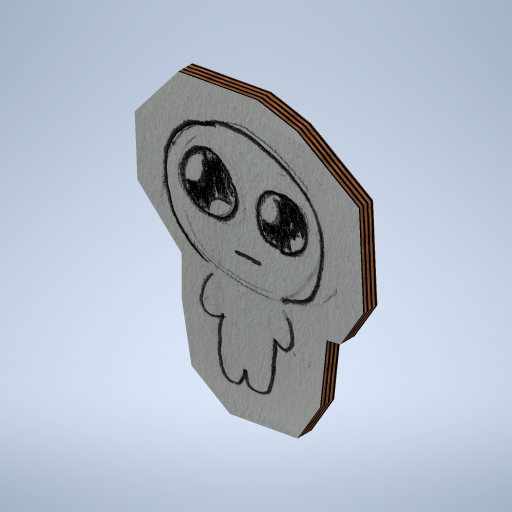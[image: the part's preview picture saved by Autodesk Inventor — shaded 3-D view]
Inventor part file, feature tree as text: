
AUTODESK INVENTOR PART (.ipt)
format: ipt  version: 2023 (Build 270158000, 158)  size: 1,415,680 bytes
history: native  units: in
note: dims shown in document units (in); Inventor stores cm internally (conversion verified against a paired STEP export)
features: extrude x1, sketch x1
ambient origin geometry x8: Origin, YZ Plane, XZ Plane, XY Plane, X Axis, Y Axis, Z Axis, Center Point
bodies: Solid1 (feature_tree)
feature tree (2):
  extrude  "Extrusion1"  Depth=1.0in
  sketch  "Sketch1"  dims[d8=1.0in d9=0.0in d11=16.107in d14=20.1844in]
